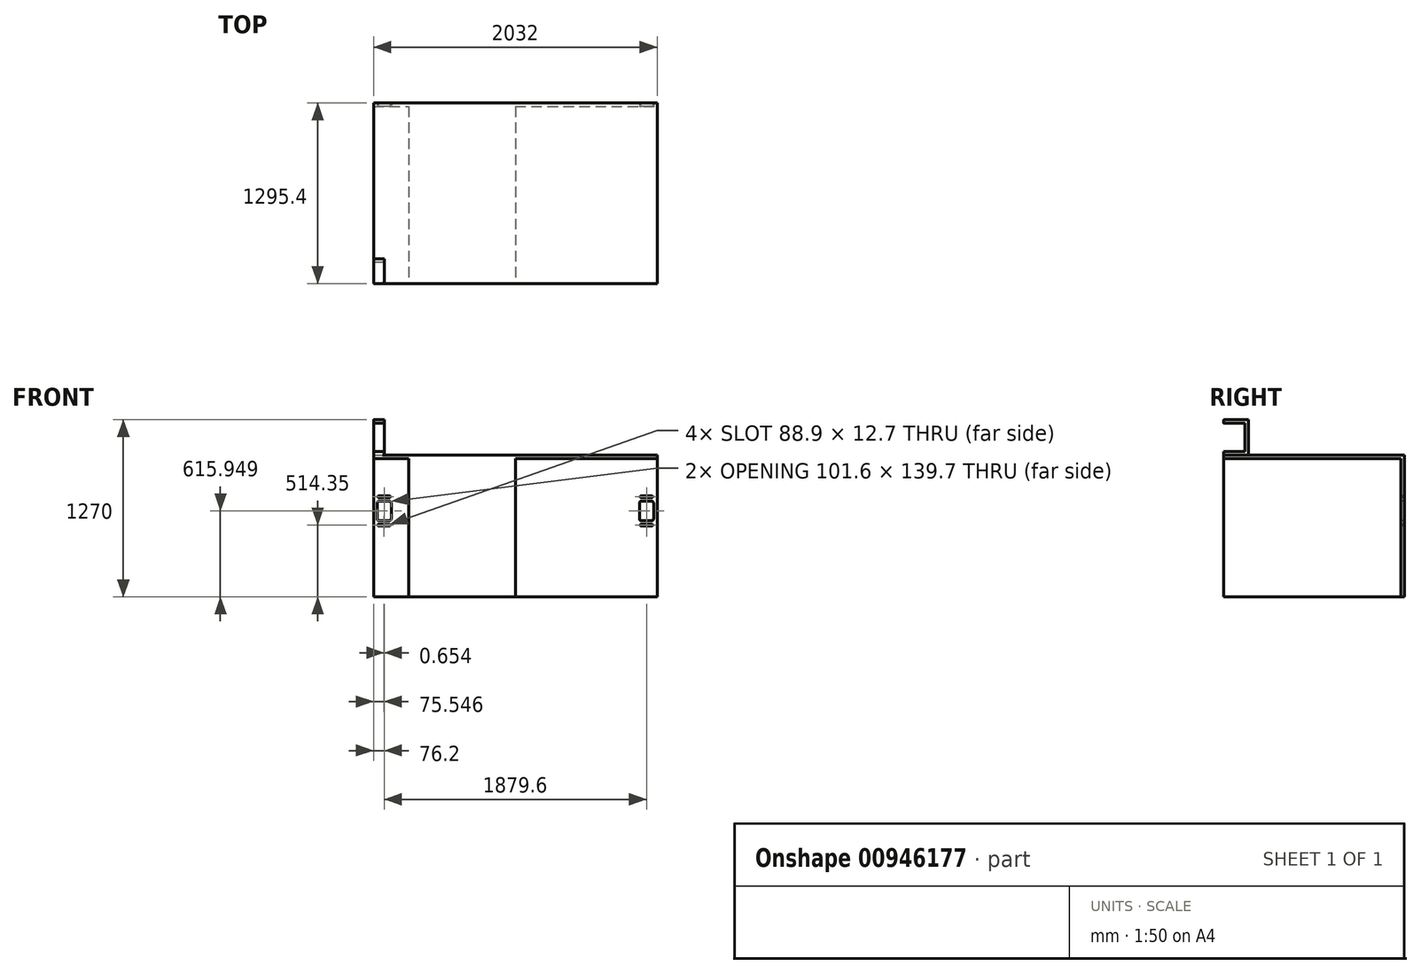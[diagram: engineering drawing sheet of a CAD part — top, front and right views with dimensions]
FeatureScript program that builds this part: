
annotation { "Feature Type Name" : "Feature", "Feature Type Description" : "" }
export const myFeature = defineFeature(function(context is Context, id is Id, definition is map)
    precondition{}
    {
        {
            var Q0;
            Q0=qCreatedBy(makeId("Front.planeOp"),FACE);
            var sketch = newSketch(context, id + "F0", { "sketchPlane" : qUnion([Q0])});
            skLineSegment(sketch, "E0.bottom", {"start": v(-762, 1162) * mm, "end": v(0, 1162) * mm});
            skLineSegment(sketch, "E0.top", {"start": v(-762, 146) * mm, "end": v(0, 146) * mm});
            skLineSegment(sketch, "E0.left", {"start": v(-762, 1162) * mm, "end": v(-762, 146) * mm});
            skLineSegment(sketch, "E0.right", {"start": v(0, 1162) * mm, "end": v(0, 146) * mm});
            skSolve(sketch);
        }
        {
            var Q0;
            Q0 = qSketchRegion(id + "F0", true);
            extrude(context, id + "F1", {"entities" : qUnion([Q0]), "depth" : 1270 * mm, "offsetDistance" : 25.4 * mm});
        }
        {
            var Q0;
            Q0=makeQuery(id+"F1.opExtrude","CAP_FACE",FACE,{"disambiguationData":[OSD([sQuery(id+"F0.wireOp",EDGE,"E0.bottom"),sQuery(id+"F0.wireOp",EDGE,"E0.top"),sQuery(id+"F0.wireOp",EDGE,"E0.left"),sQuery(id+"F0.wireOp",EDGE,"E0.right")])],"isStart":true});
            var sketch = newSketch(context, id + "F2", { "sketchPlane" : qUnion([Q0])});
            skLineSegment(sketch, "E1.bottom", {"start": v(1016, 1162) * mm, "end": v(-1016, 1162) * mm});
            skLineSegment(sketch, "E1.top", {"start": v(1016, 146) * mm, "end": v(-1016, 146) * mm});
            skLineSegment(sketch, "E1.left", {"start": v(1016, 1162) * mm, "end": v(1016, 146) * mm});
            skLineSegment(sketch, "E1.right", {"start": v(-1016, 1162) * mm, "end": v(-1016, 146) * mm});
            skSolve(sketch);
        }
        {
            var Q0;
            Q0 = qSketchRegion(id + "F2", true);
            extrude(context, id + "F3", {"entities" : qUnion([Q0]), "operationType" : NewBodyOperationType.ADD, "depth" : 25.4 * mm, "offsetDistance" : 25.4 * mm});
        }
        {
            var Q0;
            {var subQ0=sQuery(id+"F2.wireOp",EDGE,"E1.top");var subQ1=sQuery(id+"F2.wireOp",EDGE,"E1.bottom");var subQ2=sQuery(id+"F2.wireOp",EDGE,"E1.left");Q0=makeQuery(id+"F3.boolean.opBoolean","SPLIT",FACE,{"disambiguationData":[TD([makeQuery(id+"F1.opExtrude","SWEPT_FACE",FACE,{"disambiguationData":[OSD([sQuery(id+"F0.wireOp",EDGE,"E0.left")])]})])],"derivedFrom":makeQuery(id+"F3.opExtrude","CAP_FACE",FACE,{"disambiguationData":[OSD([subQ1,subQ0,subQ2,sQuery(id+"F2.wireOp",EDGE,"E1.right")])],"isStart":true})});}
            var sketch = newSketch(context, id + "F4", { "sketchPlane" : qUnion([Q0])});
            skLineSegment(sketch, "E2.bottom", {"start": v(990.6, 819.1) * mm, "end": v(990.6, 704.8) * mm});
            skLineSegment(sketch, "E2.top", {"start": v(889, 819.1) * mm, "end": v(889, 704.8) * mm});
            skLineSegment(sketch, "E2.left", {"start": v(977.9, 831.8) * mm, "end": v(901.7, 831.8) * mm});
            skLineSegment(sketch, "E2.right", {"start": v(977.9, 692.1) * mm, "end": v(901.7, 692.1) * mm});
            skLineSegment(sketch, "E3.bottom", {"start": v(984.25, 863.55) * mm, "end": v(984.25, 863.55) * mm});
            skLineSegment(sketch, "E3.top", {"start": v(895.35, 863.55) * mm, "end": v(895.35, 863.55) * mm});
            skLineSegment(sketch, "E3.left", {"start": v(977.9, 869.9) * mm, "end": v(901.7, 869.9) * mm});
            skLineSegment(sketch, "E3.right", {"start": v(977.9, 857.2) * mm, "end": v(901.7, 857.2) * mm});
            skLineSegment(sketch, "E4.bottom", {"start": v(984.25, 660.35) * mm, "end": v(984.25, 660.35) * mm});
            skLineSegment(sketch, "E4.top", {"start": v(895.35, 660.35) * mm, "end": v(895.35, 660.35) * mm});
            skLineSegment(sketch, "E4.left", {"start": v(977.9, 666.7) * mm, "end": v(901.7, 666.7) * mm});
            skLineSegment(sketch, "E4.right", {"start": v(977.9, 654) * mm, "end": v(901.7, 654) * mm});
            skPoint(sketch, "E5.visualSharp", {"position": v(984.25, 869.9) * mm});
            skArc(sketch, "E5.filletArc", {"start": v(984.25, 863.55) * mm, "mid": v(982.4, 868.04) * mm, "end": v(977.9, 869.9) * mm});
            skPoint(sketch, "E6.visualSharp", {"position": v(895.35, 857.2) * mm});
            skArc(sketch, "E6.filletArc", {"start": v(895.35, 863.55) * mm, "mid": v(897.2, 859.06) * mm, "end": v(901.7, 857.2) * mm});
            skPoint(sketch, "E7.visualSharp", {"position": v(895.35, 869.9) * mm});
            skArc(sketch, "E7.filletArc", {"start": v(901.7, 869.9) * mm, "mid": v(897.2, 868.04) * mm, "end": v(895.35, 863.55) * mm});
            skPoint(sketch, "E8.visualSharp", {"position": v(984.25, 857.2) * mm});
            skArc(sketch, "E8.filletArc", {"start": v(977.9, 857.2) * mm, "mid": v(982.4, 859.06) * mm, "end": v(984.25, 863.55) * mm});
            skPoint(sketch, "E9.visualSharp", {"position": v(990.6, 831.8) * mm});
            skArc(sketch, "E9.filletArc", {"start": v(990.6, 819.1) * mm, "mid": v(986.88, 828.08) * mm, "end": v(977.9, 831.8) * mm});
            skPoint(sketch, "E10.visualSharp", {"position": v(889, 831.8) * mm});
            skArc(sketch, "E10.filletArc", {"start": v(901.7, 831.8) * mm, "mid": v(892.72, 828.08) * mm, "end": v(889, 819.1) * mm});
            skPoint(sketch, "E11.visualSharp", {"position": v(990.6, 692.1) * mm});
            skArc(sketch, "E11.filletArc", {"start": v(977.9, 692.1) * mm, "mid": v(986.88, 695.82) * mm, "end": v(990.6, 704.8) * mm});
            skPoint(sketch, "E12.visualSharp", {"position": v(889, 692.1) * mm});
            skArc(sketch, "E12.filletArc", {"start": v(889, 704.8) * mm, "mid": v(892.72, 695.82) * mm, "end": v(901.7, 692.1) * mm});
            skPoint(sketch, "E13.visualSharp", {"position": v(984.25, 666.7) * mm});
            skArc(sketch, "E13.filletArc", {"start": v(984.25, 660.35) * mm, "mid": v(982.4, 664.84) * mm, "end": v(977.9, 666.7) * mm});
            skPoint(sketch, "E14.visualSharp", {"position": v(895.35, 654) * mm});
            skArc(sketch, "E14.filletArc", {"start": v(895.35, 660.35) * mm, "mid": v(897.2, 655.86) * mm, "end": v(901.7, 654) * mm});
            skPoint(sketch, "E15.visualSharp", {"position": v(895.35, 666.7) * mm});
            skArc(sketch, "E15.filletArc", {"start": v(901.7, 666.7) * mm, "mid": v(897.2, 664.84) * mm, "end": v(895.35, 660.35) * mm});
            skPoint(sketch, "E16.visualSharp", {"position": v(984.25, 654) * mm});
            skArc(sketch, "E16.filletArc", {"start": v(977.9, 654) * mm, "mid": v(982.4, 655.86) * mm, "end": v(984.25, 660.35) * mm});
            skLineSegment(sketch, "E17.bottom", {"start": v(-889, 819.1) * mm, "end": v(-889, 704.8) * mm});
            skLineSegment(sketch, "E17.top", {"start": v(-990.6, 819.1) * mm, "end": v(-990.6, 704.8) * mm});
            skLineSegment(sketch, "E17.left", {"start": v(-901.7, 831.8) * mm, "end": v(-977.9, 831.8) * mm});
            skLineSegment(sketch, "E17.right", {"start": v(-901.7, 692.1) * mm, "end": v(-977.9, 692.1) * mm});
            skLineSegment(sketch, "E18.bottom", {"start": v(-895.35, 863.55) * mm, "end": v(-895.35, 863.55) * mm});
            skLineSegment(sketch, "E18.top", {"start": v(-984.25, 863.55) * mm, "end": v(-984.25, 863.55) * mm});
            skLineSegment(sketch, "E18.left", {"start": v(-901.7, 869.9) * mm, "end": v(-977.9, 869.9) * mm});
            skLineSegment(sketch, "E18.right", {"start": v(-901.7, 857.2) * mm, "end": v(-977.9, 857.2) * mm});
            skLineSegment(sketch, "E19.bottom", {"start": v(-896, 660.35) * mm, "end": v(-896, 660.35) * mm});
            skLineSegment(sketch, "E19.top", {"start": v(-984.9, 660.35) * mm, "end": v(-984.9, 660.35) * mm});
            skLineSegment(sketch, "E19.left", {"start": v(-902.35, 666.7) * mm, "end": v(-978.55, 666.7) * mm});
            skLineSegment(sketch, "E19.right", {"start": v(-902.35, 654) * mm, "end": v(-978.55, 654) * mm});
            skPoint(sketch, "E20.visualSharp", {"position": v(-895.35, 869.9) * mm});
            skArc(sketch, "E20.filletArc", {"start": v(-895.35, 863.55) * mm, "mid": v(-897.2, 868.04) * mm, "end": v(-901.7, 869.9) * mm});
            skPoint(sketch, "E21.visualSharp", {"position": v(-984.25, 857.2) * mm});
            skArc(sketch, "E21.filletArc", {"start": v(-984.25, 863.55) * mm, "mid": v(-982.4, 859.06) * mm, "end": v(-977.9, 857.2) * mm});
            skPoint(sketch, "E22.visualSharp", {"position": v(-984.25, 869.9) * mm});
            skArc(sketch, "E22.filletArc", {"start": v(-977.9, 869.9) * mm, "mid": v(-982.4, 868.04) * mm, "end": v(-984.25, 863.55) * mm});
            skPoint(sketch, "E23.visualSharp", {"position": v(-895.35, 857.2) * mm});
            skArc(sketch, "E23.filletArc", {"start": v(-901.7, 857.2) * mm, "mid": v(-897.2, 859.06) * mm, "end": v(-895.35, 863.55) * mm});
            skPoint(sketch, "E24.visualSharp", {"position": v(-889, 831.8) * mm});
            skArc(sketch, "E24.filletArc", {"start": v(-889, 819.1) * mm, "mid": v(-892.72, 828.08) * mm, "end": v(-901.7, 831.8) * mm});
            skPoint(sketch, "E25.visualSharp", {"position": v(-990.6, 831.8) * mm});
            skArc(sketch, "E25.filletArc", {"start": v(-977.9, 831.8) * mm, "mid": v(-986.88, 828.08) * mm, "end": v(-990.6, 819.1) * mm});
            skPoint(sketch, "E26.visualSharp", {"position": v(-889, 692.1) * mm});
            skArc(sketch, "E26.filletArc", {"start": v(-901.7, 692.1) * mm, "mid": v(-892.72, 695.82) * mm, "end": v(-889, 704.8) * mm});
            skPoint(sketch, "E27.visualSharp", {"position": v(-990.6, 692.1) * mm});
            skArc(sketch, "E27.filletArc", {"start": v(-990.6, 704.8) * mm, "mid": v(-986.88, 695.82) * mm, "end": v(-977.9, 692.1) * mm});
            skPoint(sketch, "E28.visualSharp", {"position": v(-896, 666.7) * mm});
            skArc(sketch, "E28.filletArc", {"start": v(-896, 660.35) * mm, "mid": v(-897.86, 664.84) * mm, "end": v(-902.35, 666.7) * mm});
            skPoint(sketch, "E29.visualSharp", {"position": v(-984.9, 654) * mm});
            skArc(sketch, "E29.filletArc", {"start": v(-984.9, 660.35) * mm, "mid": v(-983.04, 655.86) * mm, "end": v(-978.55, 654) * mm});
            skPoint(sketch, "E30.visualSharp", {"position": v(-984.9, 666.7) * mm});
            skArc(sketch, "E30.filletArc", {"start": v(-978.55, 666.7) * mm, "mid": v(-983.04, 664.84) * mm, "end": v(-984.9, 660.35) * mm});
            skPoint(sketch, "E31.visualSharp", {"position": v(-896, 654) * mm});
            skArc(sketch, "E31.filletArc", {"start": v(-902.35, 654) * mm, "mid": v(-897.86, 655.86) * mm, "end": v(-896, 660.35) * mm});
            skSolve(sketch);
        }
        {
            var Q0;
            Q0 = qSketchRegion(id + "F4", true);
            extrude(context, id + "F5", {"entities" : qUnion([Q0]), "operationType" : NewBodyOperationType.REMOVE, "oppositeDirection" : true, "depth" : 25.4 * mm, "offsetDistance" : 25.4 * mm});
        }
        {
            var Q0;
            Q0=makeQuery(id+"F3.boolean.opBoolean","MERGE",FACE,{"derivedFrom":[makeQuery(id+"F1.opExtrude","SWEPT_FACE",FACE,{"disambiguationData":[OSD([sQuery(id+"F0.wireOp",EDGE,"E0.bottom")])]}),makeQuery(id+"F3.opExtrude","SWEPT_FACE",FACE,{"disambiguationData":[OSD([sQuery(id+"F2.wireOp",EDGE,"E1.bottom")])]})]});
            var sketch = newSketch(context, id + "F6", { "sketchPlane" : qUnion([Q0])});
            skLineSegment(sketch, "E32.bottom", {"start": v(-1016, 0) * mm, "end": v(1016, 0) * mm});
            skLineSegment(sketch, "E32.top", {"start": v(-1016, -1270) * mm, "end": v(1016, -1270) * mm});
            skLineSegment(sketch, "E32.left", {"start": v(-1016, 0) * mm, "end": v(-1016, -1270) * mm});
            skLineSegment(sketch, "E32.right", {"start": v(1016, 0) * mm, "end": v(1016, -1270) * mm});
            skSolve(sketch);
        }
        {
            var Q0;
            Q0 = qSketchRegion(id + "F6", true);
            extrude(context, id + "F7", {"entities" : qUnion([Q0]), "operationType" : NewBodyOperationType.ADD, "depth" : 0 * mm, "offsetDistance" : 25.4 * mm, "hasSecondDirection" : true, "secondDirectionOppositeDirection" : true, "secondDirectionDepth" : 25.4 * mm});
        }
        {
            var Q0;
            Q0=makeQuery(id+"F7.boolean.opBoolean","MERGE",FACE,{"derivedFrom":[makeQuery(id+"F3.boolean.opBoolean","MERGE",FACE,{"derivedFrom":[makeQuery(id+"F1.opExtrude","SWEPT_FACE",FACE,{"disambiguationData":[OSD([sQuery(id+"F0.wireOp",EDGE,"E0.bottom")])]}),makeQuery(id+"F3.opExtrude","SWEPT_FACE",FACE,{"disambiguationData":[OSD([sQuery(id+"F2.wireOp",EDGE,"E1.bottom")])]})]}),makeQuery(id+"F7.opExtrude","CAP_FACE",FACE,{"disambiguationData":[OSD([sQuery(id+"F6.wireOp",EDGE,"E32.bottom"),sQuery(id+"F6.wireOp",EDGE,"E32.top"),sQuery(id+"F6.wireOp",EDGE,"E32.left"),sQuery(id+"F6.wireOp",EDGE,"E32.right")])],"isStart":false})]});
            var sketch = newSketch(context, id + "F8", { "sketchPlane" : qUnion([Q0])});
            skLineSegment(sketch, "E33.bottom", {"start": v(-1003.3, -1270) * mm, "end": v(-952.5, -1270) * mm});
            skLineSegment(sketch, "E33.top", {"start": v(-1016, -1092.2) * mm, "end": v(-939.8, -1092.2) * mm});
            skLineSegment(sketch, "E33.left", {"start": v(-1016, -1257.3) * mm, "end": v(-1016, -1092.2) * mm});
            skLineSegment(sketch, "E33.right", {"start": v(-939.8, -1257.3) * mm, "end": v(-939.8, -1092.2) * mm});
            skPoint(sketch, "E34.visualSharp", {"position": v(-1016, -1270) * mm});
            skArc(sketch, "E34.filletArc", {"start": v(-1016, -1257.3) * mm, "mid": v(-1012.28, -1266.28) * mm, "end": v(-1003.3, -1270) * mm});
            skPoint(sketch, "E35.visualSharp", {"position": v(-939.8, -1270) * mm});
            skArc(sketch, "E35.filletArc", {"start": v(-952.5, -1270) * mm, "mid": v(-943.52, -1266.28) * mm, "end": v(-939.8, -1257.3) * mm});
            skSolve(sketch);
        }
        {
            var Q0;
            Q0 = qSketchRegion(id + "F8", true);
            extrude(context, id + "F9", {"entities" : qUnion([Q0]), "operationType" : NewBodyOperationType.ADD, "depth" : 254 * mm, "offsetDistance" : 25.4 * mm});
        }
        {
            var Q0;
            Q0=makeQuery(id+"F9.boolean.opBoolean","MERGE",FACE,{"derivedFrom":[makeQuery(id+"F7.boolean.opBoolean","MERGE",FACE,{"derivedFrom":[makeQuery(id+"F3.opExtrude","SWEPT_FACE",FACE,{"disambiguationData":[OSD([sQuery(id+"F2.wireOp",EDGE,"E1.left")])]}),makeQuery(id+"F7.opExtrude","SWEPT_FACE",FACE,{"disambiguationData":[OSD([sQuery(id+"F6.wireOp",EDGE,"E32.left")])]})]}),makeQuery(id+"F9.opExtrude","SWEPT_FACE",FACE,{"disambiguationData":[OSD([sQuery(id+"F8.wireOp",EDGE,"E33.left")])]})]});
            var sketch = newSketch(context, id + "F10", { "sketchPlane" : qUnion([Q0])});
            skLineSegment(sketch, "E36.bottom", {"start": v(1117.6, 1187.4) * mm, "end": v(1270, 1187.4) * mm});
            skLineSegment(sketch, "E36.top", {"start": v(1117.6, 1390.6) * mm, "end": v(1270, 1390.6) * mm});
            skLineSegment(sketch, "E36.left", {"start": v(1117.6, 1187.4) * mm, "end": v(1117.6, 1390.6) * mm});
            skLineSegment(sketch, "E36.right", {"start": v(1270, 1187.4) * mm, "end": v(1270, 1390.6) * mm});
            skSolve(sketch);
        }
        {
            var Q0;
            Q0 = qSketchRegion(id + "F10", true);
            extrude(context, id + "F11", {"entities" : qUnion([Q0]), "operationType" : NewBodyOperationType.REMOVE, "oppositeDirection" : true, "depth" : 76.2 * mm, "offsetDistance" : 25.4 * mm});
        }
    });
